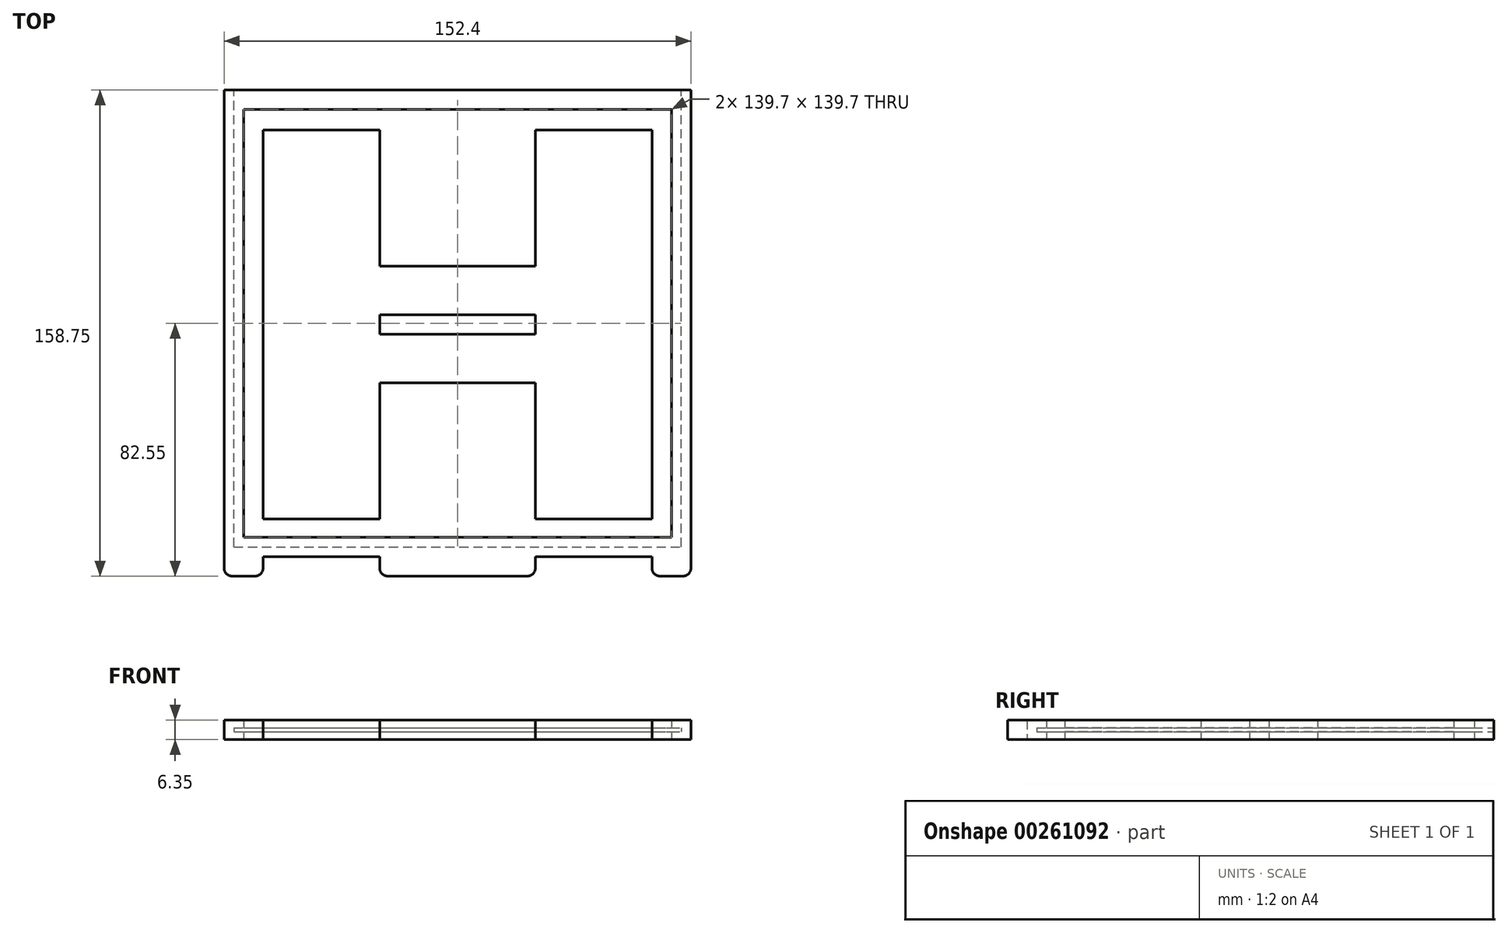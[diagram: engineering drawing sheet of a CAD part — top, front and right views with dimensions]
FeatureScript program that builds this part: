
annotation { "Feature Type Name" : "Feature", "Feature Type Description" : "" }
export const myFeature = defineFeature(function(context is Context, id is Id, definition is map)
    precondition{}
    {
        {
            var Q0;
            Q0=qCreatedBy(makeId("Top.planeOp"),FACE);
            var sketch = newSketch(context, id + "F0", { "sketchPlane" : qUnion([Q0])});
            skLineSegment(sketch, "E0.bottom", {"start": v(0, 0) * mm, "end": v(152.4, 0) * mm});
            skLineSegment(sketch, "E0.top", {"start": v(0, 158.75) * mm, "end": v(152.4, 158.75) * mm});
            skLineSegment(sketch, "E0.left", {"start": v(0, 0) * mm, "end": v(0, 158.75) * mm});
            skLineSegment(sketch, "E0.right", {"start": v(152.4, 0) * mm, "end": v(152.4, 158.75) * mm});
            skLineSegment(sketch, "E1.bottom", {"start": v(6.35, 12.7) * mm, "end": v(146.05, 12.7) * mm});
            skLineSegment(sketch, "E1.top", {"start": v(6.35, 152.4) * mm, "end": v(146.05, 152.4) * mm});
            skLineSegment(sketch, "E1.left", {"start": v(6.35, 12.7) * mm, "end": v(6.35, 152.4) * mm});
            skLineSegment(sketch, "E1.right", {"start": v(146.05, 12.7) * mm, "end": v(146.05, 152.4) * mm});
            skLineSegment(sketch, "E2.bottom", {"start": v(12.7, 0) * mm, "end": v(50.8, 0) * mm});
            skLineSegment(sketch, "E2.top", {"start": v(12.7, 6.35) * mm, "end": v(50.8, 6.35) * mm});
            skLineSegment(sketch, "E2.left", {"start": v(12.7, 0) * mm, "end": v(12.7, 6.35) * mm});
            skLineSegment(sketch, "E2.right", {"start": v(50.8, 0) * mm, "end": v(50.8, 6.35) * mm});
            skLineSegment(sketch, "E3.bottom", {"start": v(101.6, 0) * mm, "end": v(139.7, 0) * mm});
            skLineSegment(sketch, "E3.top", {"start": v(101.6, 6.35) * mm, "end": v(139.7, 6.35) * mm});
            skLineSegment(sketch, "E3.left", {"start": v(101.6, 0) * mm, "end": v(101.6, 6.35) * mm});
            skLineSegment(sketch, "E3.right", {"start": v(139.7, 0) * mm, "end": v(139.7, 6.35) * mm});
            skLineSegment(sketch, "E4.bottom", {"start": v(12.7, 145.65) * mm, "end": v(50.8, 145.65) * mm});
            skLineSegment(sketch, "E4.top", {"start": v(12.7, 18.65) * mm, "end": v(50.8, 18.65) * mm});
            skLineSegment(sketch, "E4.left", {"start": v(12.7, 145.65) * mm, "end": v(12.7, 18.65) * mm});
            skLineSegment(sketch, "E5.bottom", {"start": v(50.8, 101.2) * mm, "end": v(101.6, 101.2) * mm});
            skLineSegment(sketch, "E5.top", {"start": v(50.8, 63.1) * mm, "end": v(101.6, 63.1) * mm});
            skLineSegment(sketch, "E6.bottom", {"start": v(101.6, 145.65) * mm, "end": v(139.7, 145.65) * mm});
            skLineSegment(sketch, "E6.top", {"start": v(101.6, 18.65) * mm, "end": v(139.7, 18.65) * mm});
            skLineSegment(sketch, "E6.right", {"start": v(139.7, 145.65) * mm, "end": v(139.7, 18.65) * mm});
            skLineSegment(sketch, "E7", {"start": v(50.8, 101.2) * mm, "end": v(50.8, 145.65) * mm});
            skLineSegment(sketch, "E8", {"start": v(50.8, 63.1) * mm, "end": v(50.8, 18.65) * mm});
            skLineSegment(sketch, "E9", {"start": v(101.6, 101.2) * mm, "end": v(101.6, 145.65) * mm});
            skLineSegment(sketch, "E10", {"start": v(101.6, 63.1) * mm, "end": v(101.6, 18.65) * mm});
            skLineSegment(sketch, "E11.bottom", {"start": v(50.8, 85.33) * mm, "end": v(101.6, 85.33) * mm});
            skLineSegment(sketch, "E11.top", {"start": v(50.8, 78.98) * mm, "end": v(101.6, 78.98) * mm});
            skLineSegment(sketch, "E11.left", {"start": v(50.8, 85.33) * mm, "end": v(50.8, 78.98) * mm});
            skLineSegment(sketch, "E11.right", {"start": v(101.6, 85.33) * mm, "end": v(101.6, 78.98) * mm});
            skLineSegment(sketch, "E12", {"start": v(50.8, 85.33) * mm, "end": v(50.8, 101.2) * mm, "construction": true});
            skLineSegment(sketch, "E13", {"start": v(50.8, 63.1) * mm, "end": v(50.8, 78.98) * mm, "construction": true});
            skLineSegment(sketch, "E14", {"start": v(12.7, 6.35) * mm, "end": v(12.7, 18.65) * mm, "construction": true});
            skSolve(sketch);
        }
        {
            var Q0;
            Q0=makeQuery(id+"F0.imprint","IMPRINT",FACE,{"disambiguationData":[TD([[makeQuery(id+"F0.imprint","IMPRINT",EDGE,{"derivedFrom":sQuery(id+"F0.wireOp",EDGE,"E0.top")}),-1.0]])]});
            var Q1;
            Q1=makeQuery(id+"F0.imprint","IMPRINT",FACE,{"disambiguationData":[TD([[makeQuery(id+"F0.imprint","IMPRINT",EDGE,{"derivedFrom":sQuery(id+"F0.wireOp",EDGE,"E4.bottom")}),-1.0]])]});
            extrude(context, id + "F1", {"entities" : qUnion([Q0, Q1]), "depth" : 6.35 * mm});
        }
        {
            var Q0;
            Q0=makeQuery(id+"F1.opExtrude","SWEPT_FACE",FACE,{"disambiguationData":[OSD([sQuery(id+"F0.wireOp",EDGE,"E0.top")])]});
            var sketch = newSketch(context, id + "F2", { "sketchPlane" : qUnion([Q0])});
            skLineSegment(sketch, "E15.bottom", {"start": v(-3.17, 3.81) * mm, "end": v(-149.22, 3.81) * mm});
            skLineSegment(sketch, "E15.top", {"start": v(-3.17, 2.54) * mm, "end": v(-149.22, 2.54) * mm});
            skLineSegment(sketch, "E15.left", {"start": v(-3.17, 3.81) * mm, "end": v(-3.17, 2.54) * mm});
            skLineSegment(sketch, "E15.right", {"start": v(-149.22, 3.81) * mm, "end": v(-149.22, 2.54) * mm});
            skLineSegment(sketch, "E16", {"start": v(-3.17, 2.54) * mm, "end": v(-3.17, 0) * mm, "construction": true});
            skLineSegment(sketch, "E17", {"start": v(-3.17, 3.81) * mm, "end": v(-3.17, 6.35) * mm, "construction": true});
            skSolve(sketch);
        }
        {
            var Q0;
            Q0=makeQuery(id+"F2.imprint","IMPRINT",FACE,{"disambiguationData":[TD([[makeQuery(id+"F2.imprint","IMPRINT",EDGE,{"derivedFrom":sQuery(id+"F2.wireOp",EDGE,"E15.bottom")}),1.0]])]});
            extrude(context, id + "F3", {"entities" : qUnion([Q0]), "operationType" : NewBodyOperationType.REMOVE, "oppositeDirection" : true, "depth" : 149.22 * mm});
        }
        {
            var Q0;
            Q0=makeQuery(id+"F1.opExtrude","SWEPT_EDGE",EDGE,{"disambiguationData":[OSD([sQuery(id+"F0.wireOp",EDGE,"E0.bottom"),sQuery(id+"F0.wireOp",EDGE,"E2.bottom"),sQuery(id+"F0.wireOp",EDGE,"E2.left")])]});
            var Q1;
            Q1=makeQuery(id+"F1.opExtrude","SWEPT_EDGE",EDGE,{"disambiguationData":[OSD([sQuery(id+"F0.wireOp",EDGE,"E0.bottom"),sQuery(id+"F0.wireOp",EDGE,"E0.left")])]});
            var Q2;
            Q2=makeQuery(id+"F1.opExtrude","SWEPT_EDGE",EDGE,{"disambiguationData":[OSD([sQuery(id+"F0.wireOp",EDGE,"E0.bottom"),sQuery(id+"F0.wireOp",EDGE,"E2.bottom"),sQuery(id+"F0.wireOp",EDGE,"E2.right")])]});
            var Q3;
            Q3=makeQuery(id+"F1.opExtrude","SWEPT_EDGE",EDGE,{"disambiguationData":[OSD([sQuery(id+"F0.wireOp",EDGE,"E0.bottom"),sQuery(id+"F0.wireOp",EDGE,"E3.bottom"),sQuery(id+"F0.wireOp",EDGE,"E3.left")])]});
            var Q4;
            Q4=makeQuery(id+"F1.opExtrude","SWEPT_EDGE",EDGE,{"disambiguationData":[OSD([sQuery(id+"F0.wireOp",EDGE,"E0.bottom"),sQuery(id+"F0.wireOp",EDGE,"E3.bottom"),sQuery(id+"F0.wireOp",EDGE,"E3.right")])]});
            var Q5;
            Q5=makeQuery(id+"F1.opExtrude","SWEPT_EDGE",EDGE,{"disambiguationData":[OSD([sQuery(id+"F0.wireOp",EDGE,"E0.bottom"),sQuery(id+"F0.wireOp",EDGE,"E0.right")])]});
            fillet(context, id + "F4", {"entities" : qUnion([Q0, Q1, Q2, Q3, Q4, Q5]), "radius" : 2.54 * mm, "tangentPropagation" : true, "allowEdgeOverflow" : false});
        }
    });
